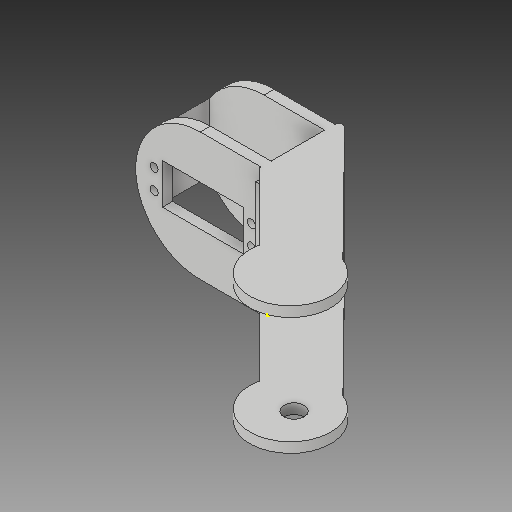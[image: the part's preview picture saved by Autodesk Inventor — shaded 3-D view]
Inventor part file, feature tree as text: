
AUTODESK INVENTOR PART (.ipt)
format: ipt  version: 2018 (Build 220112000, 112)  size: 255,488 bytes
history: native  units: mm
features: sketch x10, extrude x9, other x5, plane x3, mirror x1, fillet x1
ambient origin geometry x8: Origin, YZ Plane, XZ Plane, XY Plane, X Axis, Y Axis, Z Axis, Center Point
bodies: Solid1 (feature_tree)
feature tree (29):
  other  "Femur"
  other  "Blocks"
  plane  "Work Plane10"
  extrude  "Extrusion1"  Depth=2.0mm
  plane  "Work Plane3"
  plane  "Work Plane4"
  mirror  "Mirror3"
  extrude  "Extrusion2"  Depth=10.0mm
  sketch  "Sketch11"  dims[d21=18.5mm d22=37.0mm]
  sketch  "Sketch12"  dims[d23=5.0mm d24=0.0mm d44=5.0mm d45=0.0mm]
  extrude  "Extrusion5"  Depth=37.0mm
  extrude  "Extrusion6"  Depth=5.0mm TaperAngle=0.0deg
  extrude  "Extrusion7"  Depth=57.0mm TaperAngle=0.0deg
  extrude  "Extrusion8"  Depth=21.6mm
  extrude  "Extrusion11"  Depth=10.0mm
  extrude  "Extrusion12"  Depth=6.0mm TaperAngle=0.0deg
  extrude  "Extrusion13"  Depth=63.2mm
  fillet  "Fillet2"  Radius=63.2mm
  sketch  "Sketch4"  dims[d4=20.0mm d5=2.0mm]
  sketch  "Sketch9"  dims[d7=5.0mm d8=0.0mm d20=10.0mm]
  sketch  "Sketch13"  dims[d56=5.0mm d57=0.0mm d61=57.0mm d62=0.0mm]
  sketch  "Sketch18"  dims[d73=21.6mm d74=1.100149mm]
  sketch  "Sketch21"  dims[d75=5.0mm d76=0.0mm d85=10.0mm]
  other  "servo_frontal"
  other  "servo_con_eje"
  sketch  "Sketch28"  dims[d86=31.598344mm d87=6.0mm d88=0.0mm]
  sketch  "Sketch29"  dims[d90=5.0mm d91=0.0mm d92=14.0mm d93=63.2mm]
  sketch  "Sketch31"  dims[d94=63.2mm d95=63.2mm d96=5.0mm d97=5.0mm d98=63.2mm d99=5.0mm d100=0.0mm d101=32.0mm]
  other  "servo_frontal:1"
